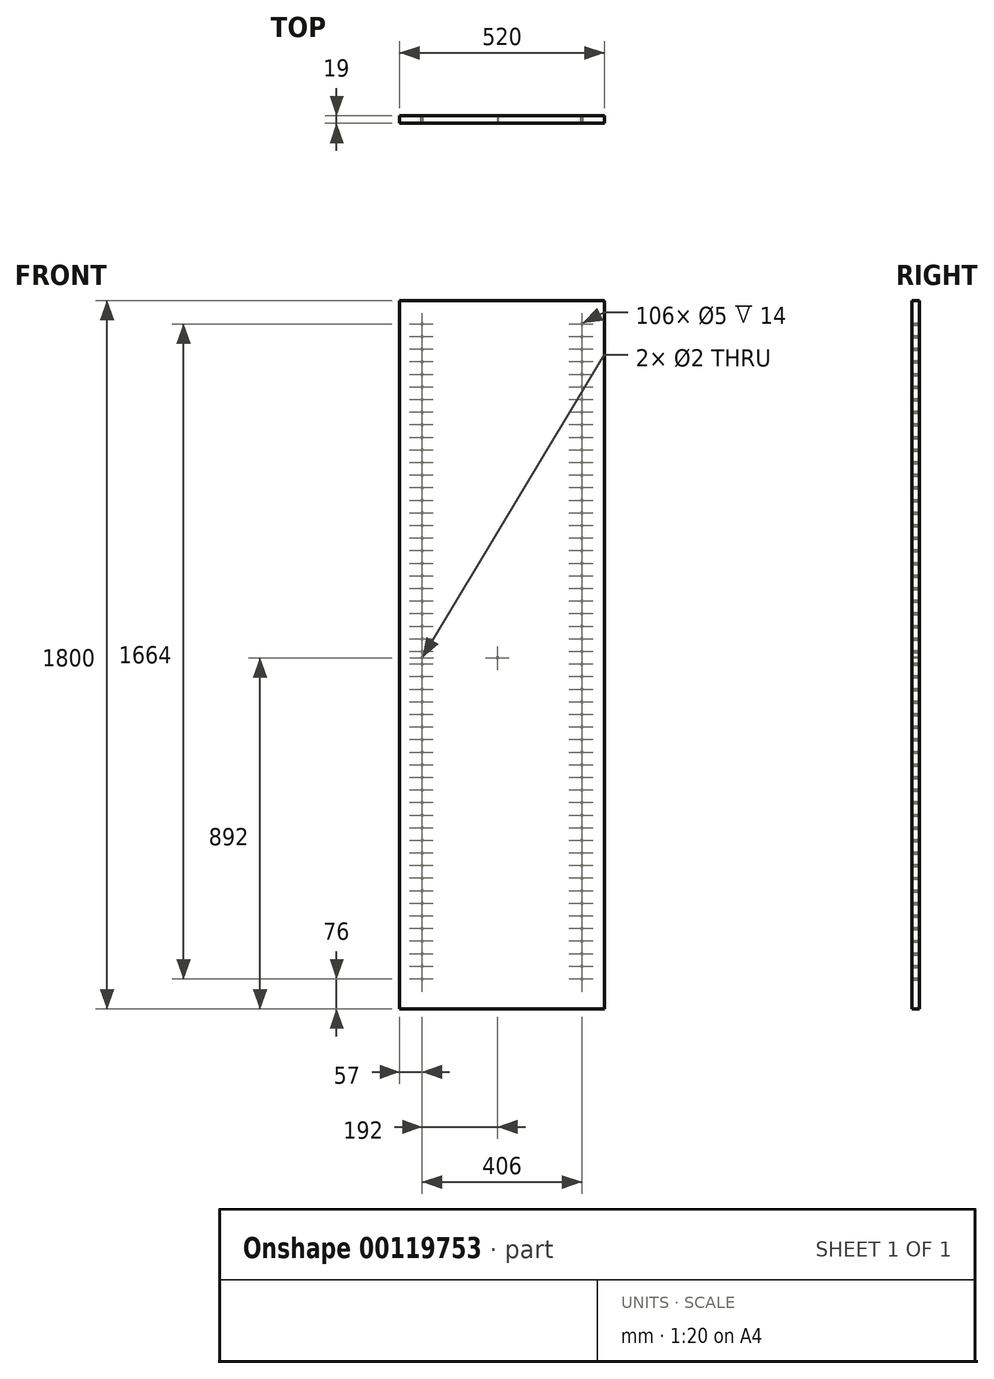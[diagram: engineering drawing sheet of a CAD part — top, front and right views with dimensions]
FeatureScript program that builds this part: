
annotation { "Feature Type Name" : "Feature", "Feature Type Description" : "" }
export const myFeature = defineFeature(function(context is Context, id is Id, definition is map)
    precondition{}
    {
        {
            var Q0;
            Q0=qCreatedBy(makeId("Front.planeOp"),FACE);
            var sketch = newSketch(context, id + "F0", { "sketchPlane" : qUnion([Q0])});
            skLineSegment(sketch, "E0.bottom", {"start": v(-260, 900) * mm, "end": v(260, 900) * mm});
            skLineSegment(sketch, "E0.top", {"start": v(-260, -900) * mm, "end": v(260, -900) * mm});
            skLineSegment(sketch, "E0.left", {"start": v(-260, 900) * mm, "end": v(-260, -900) * mm});
            skLineSegment(sketch, "E0.right", {"start": v(260, 900) * mm, "end": v(260, -900) * mm});
            skPoint(sketch, "E0.middle", {"position": v(0, 0) * mm});
            skSolve(sketch);
        }
        {
            var Q0;
            Q0=makeQuery(id+"F0.imprint","IMPRINT",FACE,{"disambiguationData":[TD([[makeQuery(id+"F0.imprint","IMPRINT",EDGE,{"derivedFrom":sQuery(id+"F0.wireOp",EDGE,"E0.bottom")}),-1.0]])]});
            extrude(context, id + "F1", {"entities" : qUnion([Q0]), "depth" : 19 * mm});
        }
        {
            var Q0;
            Q0=makeQuery(id+"F1.opExtrude","CAP_FACE",FACE,{"disambiguationData":[OSD([sQuery(id+"F0.wireOp",EDGE,"E0.bottom"),sQuery(id+"F0.wireOp",EDGE,"E0.top"),sQuery(id+"F0.wireOp",EDGE,"E0.left"),sQuery(id+"F0.wireOp",EDGE,"E0.right")])],"isStart":true});
            var sketch = newSketch(context, id + "F2", { "sketchPlane" : qUnion([Q0])});
            skCircle(sketch, "E1", {"center": v(-203, 840) * mm, "radius": 2.5 * mm});
            skCircle(sketch, "E2.0.1.0", {"center": v(-203, 808) * mm, "radius": 2.5 * mm});
            skCircle(sketch, "E2.0.2.0", {"center": v(-203, 776) * mm, "radius": 2.5 * mm});
            skCircle(sketch, "E2.0.3.0", {"center": v(-203, 744) * mm, "radius": 2.5 * mm});
            skCircle(sketch, "E2.0.4.0", {"center": v(-203, 712) * mm, "radius": 2.5 * mm});
            skCircle(sketch, "E2.0.5.0", {"center": v(-203, 680) * mm, "radius": 2.5 * mm});
            skCircle(sketch, "E2.0.6.0", {"center": v(-203, 648) * mm, "radius": 2.5 * mm});
            skCircle(sketch, "E2.0.7.0", {"center": v(-203, 616) * mm, "radius": 2.5 * mm});
            skCircle(sketch, "E2.0.8.0", {"center": v(-203, 584) * mm, "radius": 2.5 * mm});
            skCircle(sketch, "E2.0.9.0", {"center": v(-203, 552) * mm, "radius": 2.5 * mm});
            skCircle(sketch, "E2.0.10.0", {"center": v(-203, 520) * mm, "radius": 2.5 * mm});
            skCircle(sketch, "E2.0.11.0", {"center": v(-203, 488) * mm, "radius": 2.5 * mm});
            skCircle(sketch, "E2.0.12.0", {"center": v(-203, 456) * mm, "radius": 2.5 * mm});
            skCircle(sketch, "E2.0.13.0", {"center": v(-203, 424) * mm, "radius": 2.5 * mm});
            skCircle(sketch, "E2.0.14.0", {"center": v(-203, 392) * mm, "radius": 2.5 * mm});
            skCircle(sketch, "E2.0.15.0", {"center": v(-203, 360) * mm, "radius": 2.5 * mm});
            skCircle(sketch, "E2.0.16.0", {"center": v(-203, 328) * mm, "radius": 2.5 * mm});
            skCircle(sketch, "E2.0.17.0", {"center": v(-203, 296) * mm, "radius": 2.5 * mm});
            skCircle(sketch, "E2.0.18.0", {"center": v(-203, 264) * mm, "radius": 2.5 * mm});
            skCircle(sketch, "E2.0.19.0", {"center": v(-203, 232) * mm, "radius": 2.5 * mm});
            skCircle(sketch, "E2.0.20.0", {"center": v(-203, 200) * mm, "radius": 2.5 * mm});
            skCircle(sketch, "E2.0.21.0", {"center": v(-203, 168) * mm, "radius": 2.5 * mm});
            skCircle(sketch, "E2.0.22.0", {"center": v(-203, 136) * mm, "radius": 2.5 * mm});
            skCircle(sketch, "E2.0.23.0", {"center": v(-203, 104) * mm, "radius": 2.5 * mm});
            skCircle(sketch, "E2.0.24.0", {"center": v(-203, 72) * mm, "radius": 2.5 * mm});
            skCircle(sketch, "E2.0.25.0", {"center": v(-203, 40) * mm, "radius": 2.5 * mm});
            skCircle(sketch, "E2.0.26.0", {"center": v(-203, 8) * mm, "radius": 2.5 * mm});
            skCircle(sketch, "E2.0.27.0", {"center": v(-203, -24) * mm, "radius": 2.5 * mm});
            skCircle(sketch, "E2.0.28.0", {"center": v(-203, -56) * mm, "radius": 2.5 * mm});
            skCircle(sketch, "E2.0.29.0", {"center": v(-203, -88) * mm, "radius": 2.5 * mm});
            skCircle(sketch, "E2.0.30.0", {"center": v(-203, -120) * mm, "radius": 2.5 * mm});
            skCircle(sketch, "E2.0.31.0", {"center": v(-203, -152) * mm, "radius": 2.5 * mm});
            skCircle(sketch, "E2.0.32.0", {"center": v(-203, -184) * mm, "radius": 2.5 * mm});
            skCircle(sketch, "E2.0.33.0", {"center": v(-203, -216) * mm, "radius": 2.5 * mm});
            skCircle(sketch, "E2.0.34.0", {"center": v(-203, -248) * mm, "radius": 2.5 * mm});
            skCircle(sketch, "E2.0.35.0", {"center": v(-203, -280) * mm, "radius": 2.5 * mm});
            skCircle(sketch, "E2.0.36.0", {"center": v(-203, -312) * mm, "radius": 2.5 * mm});
            skCircle(sketch, "E2.0.37.0", {"center": v(-203, -344) * mm, "radius": 2.5 * mm});
            skCircle(sketch, "E2.0.38.0", {"center": v(-203, -376) * mm, "radius": 2.5 * mm});
            skCircle(sketch, "E2.0.39.0", {"center": v(-203, -408) * mm, "radius": 2.5 * mm});
            skCircle(sketch, "E2.0.40.0", {"center": v(-203, -440) * mm, "radius": 2.5 * mm});
            skCircle(sketch, "E2.0.41.0", {"center": v(-203, -472) * mm, "radius": 2.5 * mm});
            skCircle(sketch, "E2.0.42.0", {"center": v(-203, -504) * mm, "radius": 2.5 * mm});
            skCircle(sketch, "E2.0.43.0", {"center": v(-203, -536) * mm, "radius": 2.5 * mm});
            skCircle(sketch, "E2.0.44.0", {"center": v(-203, -568) * mm, "radius": 2.5 * mm});
            skCircle(sketch, "E2.0.45.0", {"center": v(-203, -600) * mm, "radius": 2.5 * mm});
            skCircle(sketch, "E2.0.46.0", {"center": v(-203, -632) * mm, "radius": 2.5 * mm});
            skCircle(sketch, "E2.0.47.0", {"center": v(-203, -664) * mm, "radius": 2.5 * mm});
            skCircle(sketch, "E2.0.48.0", {"center": v(-203, -696) * mm, "radius": 2.5 * mm});
            skCircle(sketch, "E2.0.49.0", {"center": v(-203, -728) * mm, "radius": 2.5 * mm});
            skCircle(sketch, "E2.1.0.0", {"center": v(203, 840) * mm, "radius": 2.5 * mm});
            skCircle(sketch, "E2.1.1.0", {"center": v(203, 808) * mm, "radius": 2.5 * mm});
            skCircle(sketch, "E2.1.2.0", {"center": v(203, 776) * mm, "radius": 2.5 * mm});
            skCircle(sketch, "E2.1.3.0", {"center": v(203, 744) * mm, "radius": 2.5 * mm});
            skCircle(sketch, "E2.1.4.0", {"center": v(203, 712) * mm, "radius": 2.5 * mm});
            skCircle(sketch, "E2.1.5.0", {"center": v(203, 680) * mm, "radius": 2.5 * mm});
            skCircle(sketch, "E2.1.6.0", {"center": v(203, 648) * mm, "radius": 2.5 * mm});
            skCircle(sketch, "E2.1.7.0", {"center": v(203, 616) * mm, "radius": 2.5 * mm});
            skCircle(sketch, "E2.1.8.0", {"center": v(203, 584) * mm, "radius": 2.5 * mm});
            skCircle(sketch, "E2.1.9.0", {"center": v(203, 552) * mm, "radius": 2.5 * mm});
            skCircle(sketch, "E2.1.10.0", {"center": v(203, 520) * mm, "radius": 2.5 * mm});
            skCircle(sketch, "E2.1.11.0", {"center": v(203, 488) * mm, "radius": 2.5 * mm});
            skCircle(sketch, "E2.1.12.0", {"center": v(203, 456) * mm, "radius": 2.5 * mm});
            skCircle(sketch, "E2.1.13.0", {"center": v(203, 424) * mm, "radius": 2.5 * mm});
            skCircle(sketch, "E2.1.14.0", {"center": v(203, 392) * mm, "radius": 2.5 * mm});
            skCircle(sketch, "E2.1.15.0", {"center": v(203, 360) * mm, "radius": 2.5 * mm});
            skCircle(sketch, "E2.1.16.0", {"center": v(203, 328) * mm, "radius": 2.5 * mm});
            skCircle(sketch, "E2.1.17.0", {"center": v(203, 296) * mm, "radius": 2.5 * mm});
            skCircle(sketch, "E2.1.18.0", {"center": v(203, 264) * mm, "radius": 2.5 * mm});
            skCircle(sketch, "E2.1.19.0", {"center": v(203, 232) * mm, "radius": 2.5 * mm});
            skCircle(sketch, "E2.1.20.0", {"center": v(203, 200) * mm, "radius": 2.5 * mm});
            skCircle(sketch, "E2.1.21.0", {"center": v(203, 168) * mm, "radius": 2.5 * mm});
            skCircle(sketch, "E2.1.22.0", {"center": v(203, 136) * mm, "radius": 2.5 * mm});
            skCircle(sketch, "E2.1.23.0", {"center": v(203, 104) * mm, "radius": 2.5 * mm});
            skCircle(sketch, "E2.1.24.0", {"center": v(203, 72) * mm, "radius": 2.5 * mm});
            skCircle(sketch, "E2.1.25.0", {"center": v(203, 40) * mm, "radius": 2.5 * mm});
            skCircle(sketch, "E2.1.26.0", {"center": v(203, 8) * mm, "radius": 2.5 * mm});
            skCircle(sketch, "E2.1.27.0", {"center": v(203, -24) * mm, "radius": 2.5 * mm});
            skCircle(sketch, "E2.1.28.0", {"center": v(203, -56) * mm, "radius": 2.5 * mm});
            skCircle(sketch, "E2.1.29.0", {"center": v(203, -88) * mm, "radius": 2.5 * mm});
            skCircle(sketch, "E2.1.30.0", {"center": v(203, -120) * mm, "radius": 2.5 * mm});
            skCircle(sketch, "E2.1.31.0", {"center": v(203, -152) * mm, "radius": 2.5 * mm});
            skCircle(sketch, "E2.1.32.0", {"center": v(203, -184) * mm, "radius": 2.5 * mm});
            skCircle(sketch, "E2.1.33.0", {"center": v(203, -216) * mm, "radius": 2.5 * mm});
            skCircle(sketch, "E2.1.34.0", {"center": v(203, -248) * mm, "radius": 2.5 * mm});
            skCircle(sketch, "E2.1.35.0", {"center": v(203, -280) * mm, "radius": 2.5 * mm});
            skCircle(sketch, "E2.1.36.0", {"center": v(203, -312) * mm, "radius": 2.5 * mm});
            skCircle(sketch, "E2.1.37.0", {"center": v(203, -344) * mm, "radius": 2.5 * mm});
            skCircle(sketch, "E2.1.38.0", {"center": v(203, -376) * mm, "radius": 2.5 * mm});
            skCircle(sketch, "E2.1.39.0", {"center": v(203, -408) * mm, "radius": 2.5 * mm});
            skCircle(sketch, "E2.1.40.0", {"center": v(203, -440) * mm, "radius": 2.5 * mm});
            skCircle(sketch, "E2.1.41.0", {"center": v(203, -472) * mm, "radius": 2.5 * mm});
            skCircle(sketch, "E2.1.42.0", {"center": v(203, -504) * mm, "radius": 2.5 * mm});
            skCircle(sketch, "E2.1.43.0", {"center": v(203, -536) * mm, "radius": 2.5 * mm});
            skCircle(sketch, "E2.1.44.0", {"center": v(203, -568) * mm, "radius": 2.5 * mm});
            skCircle(sketch, "E2.1.45.0", {"center": v(203, -600) * mm, "radius": 2.5 * mm});
            skCircle(sketch, "E2.1.46.0", {"center": v(203, -632) * mm, "radius": 2.5 * mm});
            skCircle(sketch, "E2.1.47.0", {"center": v(203, -664) * mm, "radius": 2.5 * mm});
            skCircle(sketch, "E2.1.48.0", {"center": v(203, -696) * mm, "radius": 2.5 * mm});
            skCircle(sketch, "E2.1.49.0", {"center": v(203, -728) * mm, "radius": 2.5 * mm});
            skLineSegment(sketch, "E2.direction1", {"start": v(-203, 840) * mm, "end": v(203, 840) * mm, "construction": true});
            skLineSegment(sketch, "E2.direction2", {"start": v(-203, 840) * mm, "end": v(-203, 808) * mm, "construction": true});
            skCircle(sketch, "E3.0.0.50", {"center": v(-203, -760) * mm, "radius": 2.5 * mm});
            skCircle(sketch, "E3.0.0.51", {"center": v(-203, -792) * mm, "radius": 2.5 * mm});
            skCircle(sketch, "E3.0.0.52", {"center": v(-203, -824) * mm, "radius": 2.5 * mm});
            skCircle(sketch, "E3.0.1.50", {"center": v(203, -760) * mm, "radius": 2.5 * mm});
            skCircle(sketch, "E3.0.1.51", {"center": v(203, -792) * mm, "radius": 2.5 * mm});
            skCircle(sketch, "E3.0.1.52", {"center": v(203, -824) * mm, "radius": 2.5 * mm});
            skSolve(sketch);
        }
        {
            var Q0;
            Q0=qSketchRegion(id+"F2",true);
            extrude(context, id + "F3", {"entities" : qUnion([Q0]), "operationType" : NewBodyOperationType.REMOVE, "oppositeDirection" : true, "depth" : 14 * mm});
        }
        {
            var Q0;
            Q0=makeQuery(id+"F1.opExtrude","CAP_FACE",FACE,{"disambiguationData":[OSD([sQuery(id+"F0.wireOp",EDGE,"E0.bottom"),sQuery(id+"F0.wireOp",EDGE,"E0.top"),sQuery(id+"F0.wireOp",EDGE,"E0.left"),sQuery(id+"F0.wireOp",EDGE,"E0.right")])],"isStart":false});
            var sketch = newSketch(context, id + "F4", { "sketchPlane" : qUnion([Q0])});
            skLineSegment(sketch, "E4", {"start": v(-203, -8) * mm, "end": v(-11, -8) * mm, "construction": true});
            skCircle(sketch, "E5", {"center": v(-203, -8) * mm, "radius": 1 * mm});
            skCircle(sketch, "E6", {"center": v(-11, -8) * mm, "radius": 1 * mm});
            skSolve(sketch);
        }
        {
            var Q0;
            Q0=qSketchRegion(id+"F4",true);
            extrude(context, id + "F5", {"entities" : qUnion([Q0]), "operationType" : NewBodyOperationType.REMOVE, "oppositeDirection" : true, "depth" : 25 * mm});
        }
    });
